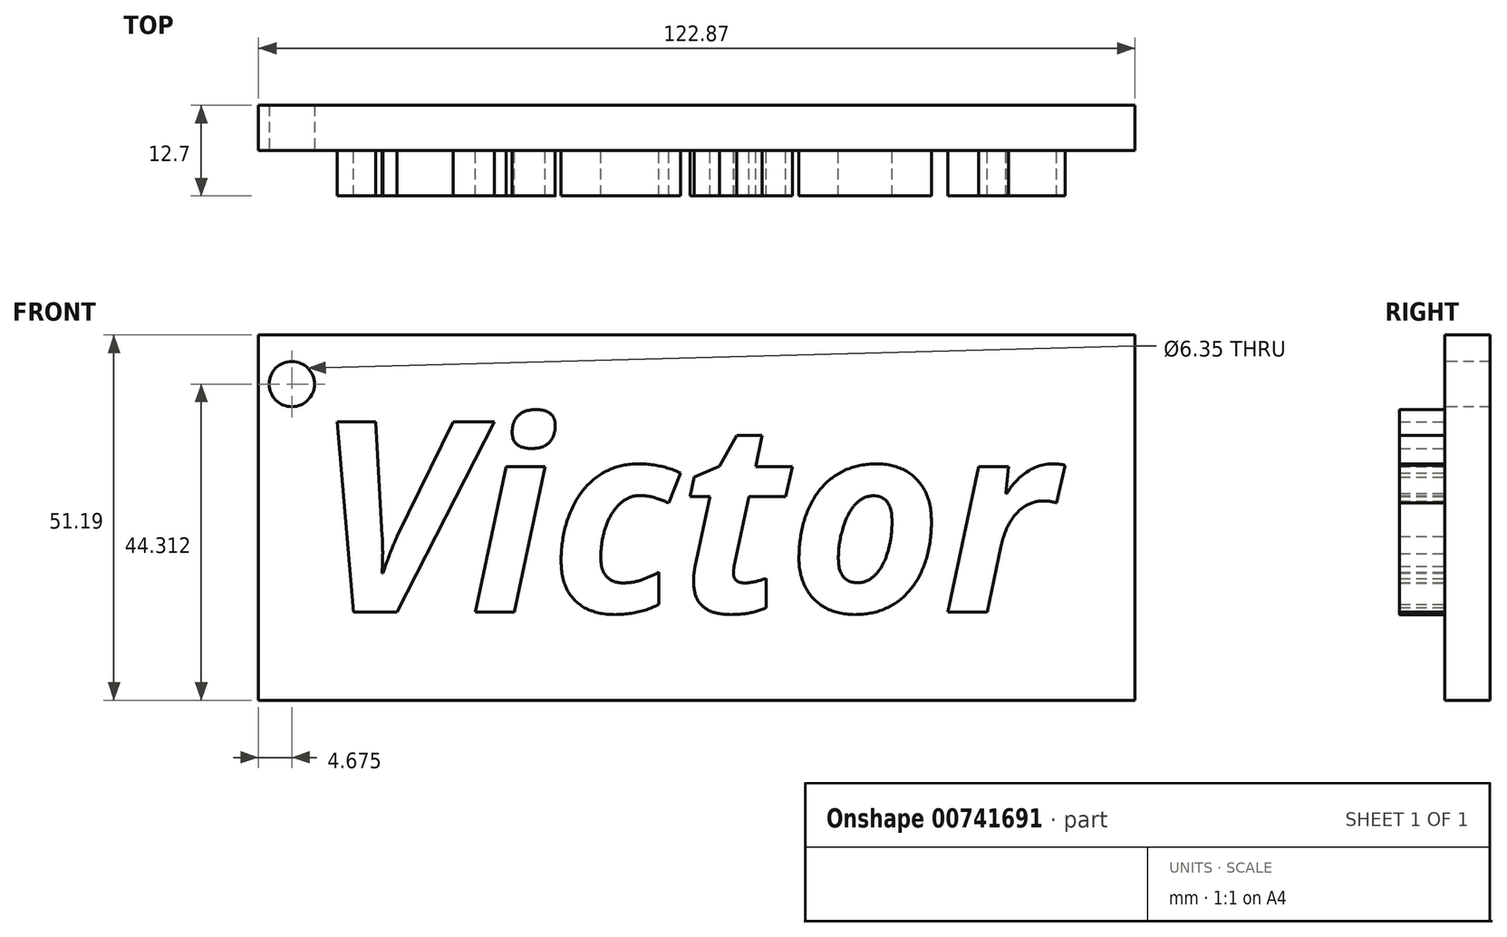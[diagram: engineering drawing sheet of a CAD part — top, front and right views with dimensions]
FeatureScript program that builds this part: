
annotation { "Feature Type Name" : "Feature", "Feature Type Description" : "" }
export const myFeature = defineFeature(function(context is Context, id is Id, definition is map)
    precondition{}
    {
        {
            var Q0;
            Q0=qCreatedBy(makeId("Front.planeOp"),FACE);
            var sketch = newSketch(context, id + "F0", { "sketchPlane" : qUnion([Q0])});
            skLineSegment(sketch, "E0.bottom", {"start": v(-57.8, 28.58) * mm, "end": v(65.06, 28.58) * mm});
            skLineSegment(sketch, "E0.top", {"start": v(-57.8, -22.61) * mm, "end": v(65.06, -22.61) * mm});
            skLineSegment(sketch, "E0.left", {"start": v(-57.8, 28.58) * mm, "end": v(-57.8, -22.61) * mm});
            skLineSegment(sketch, "E0.right", {"start": v(65.06, 28.58) * mm, "end": v(65.06, -22.61) * mm});
            skSolve(sketch);
        }
        {
            var Q0;
            Q0=makeQuery(id+"F0.imprint","IMPRINT",FACE,{"disambiguationData":[TD([[makeQuery(id+"F0.imprint","IMPRINT",EDGE,{"derivedFrom":sQuery(id+"F0.wireOp",EDGE,"E0.bottom")}),-1.0]])]});
            extrude(context, id + "F1", {"entities" : qUnion([Q0]), "depth" : 6.35 * mm, "offsetDistance" : 25.4 * mm});
        }
        {
            var Q0;
            Q0=makeQuery(id+"F1.opExtrude","CAP_FACE",FACE,{"disambiguationData":[OSD([sQuery(id+"F0.wireOp",EDGE,"E0.bottom"),sQuery(id+"F0.wireOp",EDGE,"E0.top"),sQuery(id+"F0.wireOp",EDGE,"E0.left"),sQuery(id+"F0.wireOp",EDGE,"E0.right")])],"isStart":false});
            var sketch = newSketch(context, id + "F2", { "sketchPlane" : qUnion([Q0])});
            skText(sketch, "E1", { "text": "Victor", "fontName": "OpenSans-BoldItalic.ttf"});
            const initialGuessF2  = {"E1": [-0.05013, -0.01024, 1, 0, 0.02688]};
            skSetInitialGuess(sketch, initialGuessF2);
            skSolve(sketch);
        }
        {
            var Q0;
            Q0 = qSketchRegion(id + "F2", true);
            var Q1;
            Q1 = qConstructionFilter(qBodyType(qCreatedBy(id + "F2" ,EDGE), BodyType.WIRE), ConstructionObject.NO);
            extrude(context, id + "F3", {"entities" : qUnion([Q0]), "operationType" : NewBodyOperationType.ADD, "surfaceEntities" : qUnion([Q1]), "depth" : 6.35 * mm, "offsetDistance" : 25.4 * mm});
        }
        {
            var Q0;
            Q0=makeQuery(id+"F1.opExtrude","CAP_FACE",FACE,{"disambiguationData":[OSD([sQuery(id+"F0.wireOp",EDGE,"E0.bottom"),sQuery(id+"F0.wireOp",EDGE,"E0.top"),sQuery(id+"F0.wireOp",EDGE,"E0.left"),sQuery(id+"F0.wireOp",EDGE,"E0.right")])],"isStart":false});
            var sketch = newSketch(context, id + "F4", { "sketchPlane" : qUnion([Q0])});
            skCircle(sketch, "E2", {"center": v(-53.14, 21.7) * mm, "radius": 4.4 * mm});
            skCircle(sketch, "E3", {"center": v(-53.14, 21.7) * mm, "radius": 2.81 * mm});
            skSolve(sketch);
        }
        {
            var Q0;
            Q0=sQuery(id+"F4.wireOp",VERTEX,"E2.center");
            var Q1;
            Q1=makeQuery(id+"F1.opExtrude","SWEPT_BODY",BODY,{"disambiguationData":[OSD([sQuery(id+"F0.wireOp",EDGE,"E0.bottom"),sQuery(id+"F0.wireOp",EDGE,"E0.top"),sQuery(id+"F0.wireOp",EDGE,"E0.left"),sQuery(id+"F0.wireOp",EDGE,"E0.right")])]});
            hole(context, id + "F5", {"style" : HoleStyle.SIMPLE, "endStyle" : HoleEndStyle.THROUGH, "holeDiameter" : 6.35 * mm, "majorDiameter" : 6.35 * mm, "isTappedThrough" : true, "tappedDepth" : 12.7 * mm, "tapClearance" : 3, "locations" : qUnion([Q0]), "scope" : qUnion([Q1])});
        }
    });
